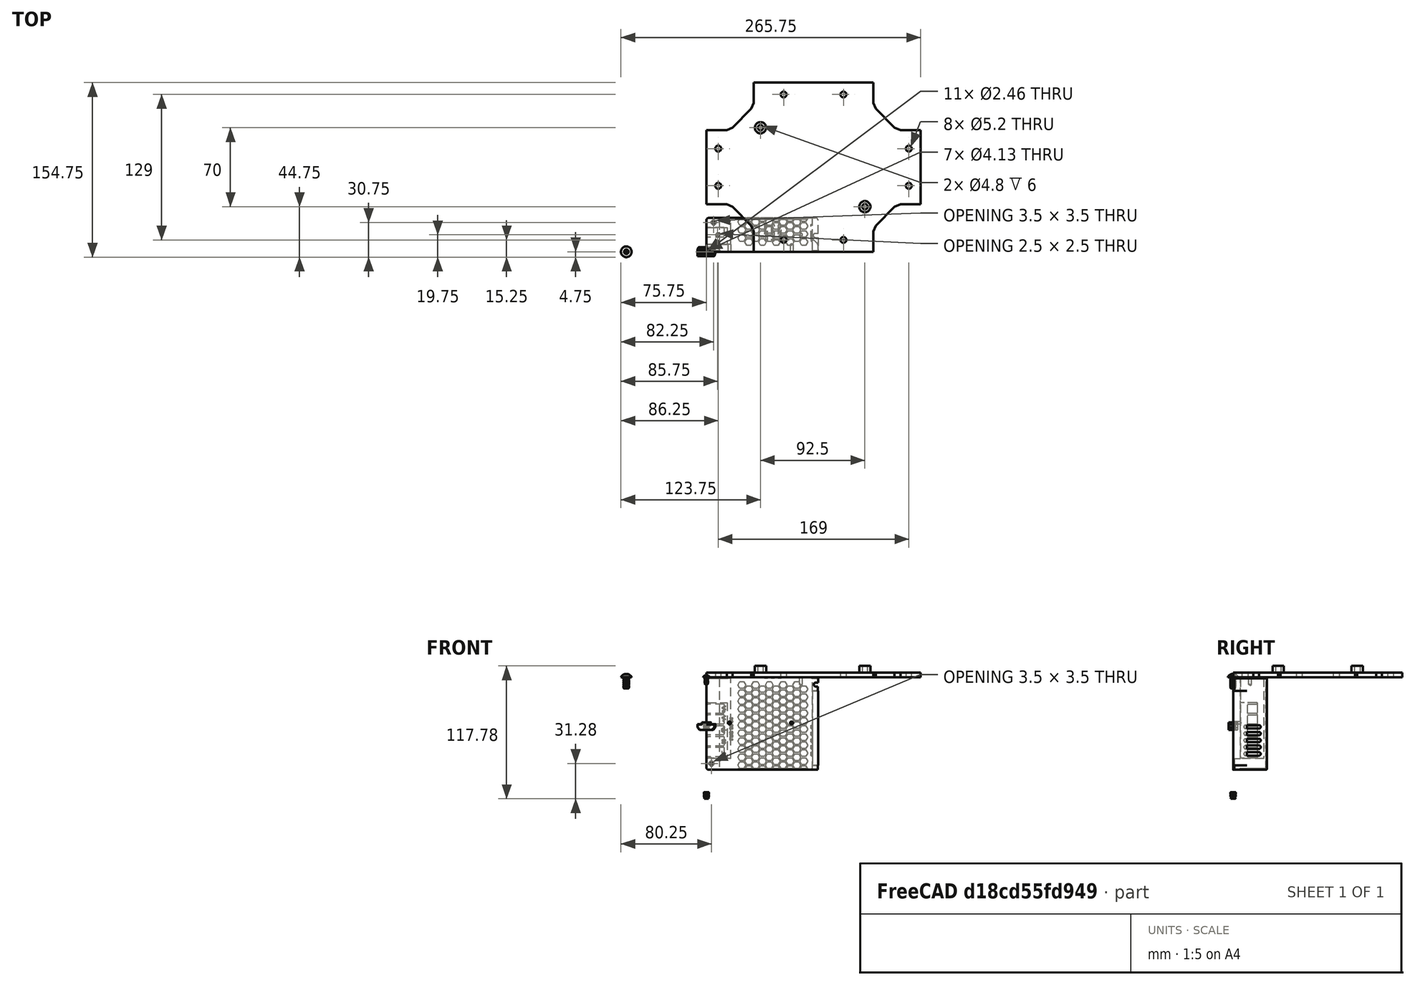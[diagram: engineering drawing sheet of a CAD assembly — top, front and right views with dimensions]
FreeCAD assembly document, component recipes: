
FREECAD ASSEMBLY — COMPONENT RECIPES ("psu-mount")

This assembly document has 14 components, labeled P0..P13 below (a component is one placed body or linked part). 1 of them carries a construction recipe — the FreeCAD feature program that regenerates the part from scratch, quoted from this document or its linked companion documents; the rest are supplied as boundary geometry only. No exploded tour is included for this assembly.
COMPONENT P0 — geometry summary ("M3x5.74-Insert001"; no construction recipe available for this part):
  bounding box: 5.7 x 4.6 x 4.5 mm
  tessellated surface: 13,418 triangles
  volume: 43 mm^3 (36% of its bounding box)
COMPONENT P1 — geometry summary ("M3x5.74-Insert002"; no construction recipe available for this part):
  bounding box: 5.7 x 4.6 x 4.5 mm
  tessellated surface: 13,418 triangles
  volume: 43 mm^3 (36% of its bounding box)
COMPONENT P2 — geometry summary ("M3x6-Screw001"; no construction recipe available for this part):
  bounding box: 7.6 x 5.7 x 5.7 mm
  tessellated surface: 15,240 triangles
  volume: 57 mm^3 (23% of its bounding box)
COMPONENT P3 — geometry summary ("M3x6-Screw002"; no construction recipe available for this part):
  bounding box: 7.6 x 5.7 x 5.7 mm
  tessellated surface: 15,240 triangles
  volume: 57 mm^3 (23% of its bounding box)
COMPONENT P4 — geometry summary ("M5x10-Screw001"; no construction recipe available for this part):
  bounding box: 12.8 x 9.5 x 9.5 mm
  tessellated surface: 23,732 triangles
  volume: 267 mm^3 (23% of its bounding box)
  symmetry: revolution-symmetric about the z axis through its bounding-box center
COMPONENT P5 — geometry summary ("M5x10-Screw003"; no construction recipe available for this part):
  bounding box: 12.8 x 9.5 x 9.5 mm
  tessellated surface: 23,732 triangles
  volume: 267 mm^3 (23% of its bounding box)
  symmetry: revolution-symmetric about the z axis through its bounding-box center
COMPONENT P6 — geometry summary ("M5x10-Screw004"; no construction recipe available for this part):
  bounding box: 12.8 x 9.5 x 9.5 mm
  tessellated surface: 23,732 triangles
  volume: 267 mm^3 (23% of its bounding box)
  symmetry: revolution-symmetric about the z axis through its bounding-box center
COMPONENT P7 — geometry summary ("M5x10-Screw005"; no construction recipe available for this part):
  bounding box: 12.8 x 9.5 x 9.5 mm
  tessellated surface: 23,732 triangles
  volume: 267 mm^3 (23% of its bounding box)
  symmetry: revolution-symmetric about the z axis through its bounding-box center
COMPONENT P8 — geometry summary ("M5x10-Screw006"; no construction recipe available for this part):
  bounding box: 12.8 x 9.5 x 9.5 mm
  tessellated surface: 23,732 triangles
  volume: 267 mm^3 (23% of its bounding box)
  symmetry: revolution-symmetric about the z axis through its bounding-box center
COMPONENT P9 — geometry summary ("M5x10-Screw007"; no construction recipe available for this part):
  bounding box: 12.8 x 9.5 x 9.5 mm
  tessellated surface: 23,732 triangles
  volume: 267 mm^3 (23% of its bounding box)
  symmetry: revolution-symmetric about the z axis through its bounding-box center
COMPONENT P10 — geometry summary ("M5x10-Screw008"; no construction recipe available for this part):
  bounding box: 12.8 x 9.5 x 9.5 mm
  tessellated surface: 23,732 triangles
  volume: 267 mm^3 (23% of its bounding box)
  symmetry: revolution-symmetric about the z axis through its bounding-box center
COMPONENT P11 — geometry summary ("M5x10-Screw009"; no construction recipe available for this part):
  bounding box: 12.8 x 9.5 x 9.5 mm
  tessellated surface: 23,732 triangles
  volume: 267 mm^3 (23% of its bounding box)
  symmetry: revolution-symmetric about the z axis through its bounding-box center
COMPONENT P12 — geometry summary ("MW LRS-50-025"; no construction recipe available for this part):
  bounding box: 99.0 x 82.0 x 30.0 mm
  tessellated surface: 16,878 triangles
  volume: 199954 mm^3 (82% of its bounding box)
COMPONENT P13 — recipe-attached ("mount001", modeled in this document).
Construction recipe (the document's own serialized feature program — sketch geometry with constraints, then the solid features built on it; lengths are millimeters unless a unit is written):

FEATURE [Sketcher::SketchObject] Sketch
  ArcFitTolerance = 1e-06
  AttachmentSupport = -> [XY_Plane]
  FullyConstrained = true
  MakeInternals = false
  MapMode = 5
  sketch-geometry (56):
    g0: LineSegment [constr] StartX=0 StartY=0 StartZ=0 EndX=190 EndY=0 EndZ=0
    g1: LineSegment [constr] StartX=190 StartY=0 StartZ=0 EndX=190 EndY=150 EndZ=0
    g2: LineSegment [constr] StartX=190 StartY=150 StartZ=0 EndX=0 EndY=150 EndZ=0
    g3: LineSegment [constr] StartX=0 StartY=150 StartZ=0 EndX=0 EndY=0 EndZ=0
    g4: LineSegment [constr] StartX=0 StartY=0 StartZ=0 EndX=42 EndY=0 EndZ=0
    g5: LineSegment [constr] StartX=42 StartY=0 StartZ=0 EndX=42 EndY=42 EndZ=0
    g6: LineSegment [constr] StartX=42 StartY=42 StartZ=0 EndX=0 EndY=42 EndZ=0
    g7: LineSegment [constr] StartX=0 StartY=42 StartZ=0 EndX=0 EndY=0 EndZ=0
    g8: LineSegment [constr] StartX=0 StartY=150 StartZ=0 EndX=0 EndY=108 EndZ=0
    g9: LineSegment [constr] StartX=0 StartY=108 StartZ=0 EndX=42 EndY=108 EndZ=0
    g10: LineSegment [constr] StartX=42 StartY=108 StartZ=0 EndX=42 EndY=150 EndZ=0
    g11: LineSegment [constr] StartX=42 StartY=150 StartZ=0 EndX=0 EndY=150 EndZ=0
    g12: LineSegment [constr] StartX=190 StartY=150 StartZ=0 EndX=148 EndY=150 EndZ=0
    g13: LineSegment [constr] StartX=148 StartY=150 StartZ=0 EndX=148 EndY=108 EndZ=0
    g14: LineSegment [constr] StartX=148 StartY=108 StartZ=0 EndX=190 EndY=108 EndZ=0
    g15: LineSegment [constr] StartX=190 StartY=108 StartZ=0 EndX=190 EndY=150 EndZ=0
    g16: LineSegment [constr] StartX=190 StartY=0 StartZ=0 EndX=190 EndY=42 EndZ=0
    g17: LineSegment [constr] StartX=190 StartY=42 StartZ=0 EndX=148 EndY=42 EndZ=0
    g18: LineSegment [constr] StartX=148 StartY=42 StartZ=0 EndX=148 EndY=0 EndZ=0
    g19: LineSegment [constr] StartX=148 StartY=0 StartZ=0 EndX=190 EndY=0 EndZ=0
    g20: LineSegment StartX=42 StartY=129 StartZ=0 EndX=21 EndY=108 EndZ=0
    g21: LineSegment StartX=21 StartY=108 StartZ=0 EndX=0 EndY=108 EndZ=0
    g22: LineSegment StartX=0 StartY=108 StartZ=0 EndX=0 EndY=42 EndZ=0
    g23: LineSegment StartX=0 StartY=42 StartZ=0 EndX=21 EndY=42 EndZ=0
    g24: LineSegment StartX=21 StartY=42 StartZ=0 EndX=42 EndY=21 EndZ=0
    g25: LineSegment StartX=42 StartY=21 StartZ=0 EndX=42 EndY=0 EndZ=0
    g26: LineSegment StartX=42 StartY=0 StartZ=0 EndX=148 EndY=0 EndZ=0
    g27: LineSegment StartX=148 StartY=0 StartZ=0 EndX=148 EndY=21 EndZ=0
    g28: LineSegment StartX=148 StartY=21 StartZ=0 EndX=169 EndY=42 EndZ=0
    g29: LineSegment StartX=169 StartY=42 StartZ=0 EndX=190 EndY=42 EndZ=0
    g30: LineSegment StartX=190 StartY=42 StartZ=0 EndX=190 EndY=108 EndZ=0
    g31: LineSegment StartX=190 StartY=108 StartZ=0 EndX=169 EndY=108 EndZ=0
    g32: LineSegment StartX=169 StartY=108 StartZ=0 EndX=148 EndY=129 EndZ=0
    g33: LineSegment StartX=148 StartY=129 StartZ=0 EndX=148 EndY=150 EndZ=0
    g34: LineSegment StartX=148 StartY=150 StartZ=0 EndX=42 EndY=150 EndZ=0
    g35: LineSegment StartX=42 StartY=150 StartZ=0 EndX=42 EndY=129 EndZ=0
    g36: LineSegment [constr] StartX=95 StartY=129 StartZ=0 EndX=95 EndY=150 EndZ=0
    g37: LineSegment [constr] StartX=95 StartY=139.5 StartZ=0 EndX=42 EndY=139.5 EndZ=0
    g38: Circle CenterX=68.5 CenterY=139.5 CenterZ=0 NormalX=0 NormalY=0 NormalZ=1 AngleXU=0 Radius=2.6
    g39: LineSegment [constr] StartX=95 StartY=139.5 StartZ=0 EndX=148 EndY=139.5 EndZ=0
    g40: Circle CenterX=121.5 CenterY=139.5 CenterZ=0 NormalX=0 NormalY=0 NormalZ=1 AngleXU=0 Radius=2.6
    g41: LineSegment [constr] StartX=0 StartY=75 StartZ=0 EndX=21 EndY=75 EndZ=0
    g42: LineSegment [constr] StartX=10.5 StartY=75 StartZ=0 EndX=10.5 EndY=108 EndZ=0
    g43: LineSegment [constr] StartX=10.5 StartY=75 StartZ=0 EndX=10.5 EndY=42 EndZ=0
    g44: Circle CenterX=10.5 CenterY=91.5 CenterZ=0 NormalX=0 NormalY=0 NormalZ=1 AngleXU=0 Radius=2.6
    g45: Circle CenterX=10.5 CenterY=58.5 CenterZ=0 NormalX=0 NormalY=0 NormalZ=1 AngleXU=0 Radius=2.6
    g46: LineSegment [constr] StartX=95 StartY=21 StartZ=0 EndX=95 EndY=0 EndZ=0
    g47: LineSegment [constr] StartX=95 StartY=10.5 StartZ=0 EndX=42 EndY=10.5 EndZ=0
    g48: LineSegment [constr] StartX=95 StartY=10.5 StartZ=0 EndX=148 EndY=10.5 EndZ=0
    g49: Circle CenterX=68.5 CenterY=10.5 CenterZ=0 NormalX=0 NormalY=0 NormalZ=1 AngleXU=0 Radius=2.6
    g50: Circle CenterX=121.5 CenterY=10.5 CenterZ=0 NormalX=0 NormalY=0 NormalZ=1 AngleXU=0 Radius=2.6
    g51: LineSegment [constr] StartX=169 StartY=75 StartZ=0 EndX=190 EndY=75 EndZ=0
    g52: LineSegment [constr] StartX=179.5 StartY=75 StartZ=0 EndX=179.5 EndY=42 EndZ=0
    g53: LineSegment [constr] StartX=179.5 StartY=75 StartZ=0 EndX=179.5 EndY=108 EndZ=0
    g54: Circle CenterX=179.5 CenterY=91.5 CenterZ=0 NormalX=0 NormalY=0 NormalZ=1 AngleXU=0 Radius=2.6
    g55: Circle CenterX=179.5 CenterY=58.5 CenterZ=0 NormalX=0 NormalY=0 NormalZ=1 AngleXU=0 Radius=2.6
  constraints (127):
    c: Coincident(g0,g1)
    c: Coincident(g1,g2)
    c: Coincident(g2,g3)
    c: Coincident(g3,g0)
    c: Horizontal(g0)
    c: Horizontal(g2)
    c: Vertical(g1)
    c: Vertical(g3)
    c: Distance(g1,g3) = 190
    c: Distance(g0,g2) = 150
    c: Coincident(g0,g-1)
    c: Coincident(g4,g5)
    c: Coincident(g5,g6)
    c: Coincident(g6,g7)
    c: Coincident(g7,g4)
    c: Horizontal(g4)
    c: Horizontal(g6)
    c: Vertical(g5)
    c: Vertical(g7)
    c: Distance(g5,g7) = 42
    c: Distance(g4,g6) = 42
    c: Coincident(g4,g0)
    c: Coincident(g8,g9)
    c: Coincident(g9,g10)
    c: Coincident(g10,g11)
    c: Coincident(g11,g8)
    c: Vertical(g8)
    c: Vertical(g10)
    c: Horizontal(g9)
    c: Horizontal(g11)
    c: Distance(g8,g10) = 42
    c: Distance(g9,g11) = 42
    c: Coincident(g8,g2)
    c: Coincident(g12,g13)
    c: Coincident(g13,g14)
    c: Coincident(g14,g15)
    c: Coincident(g15,g12)
    c: Horizontal(g12)
    c: Horizontal(g14)
    c: Vertical(g13)
    c: Vertical(g15)
    c: Distance(g13,g15) = 42
    c: Distance(g12,g14) = 42
    c: Coincident(g12,g1)
    c: Coincident(g16,g17)
    c: Coincident(g17,g18)
    c: Coincident(g18,g19)
    c: Coincident(g19,g16)
    c: Vertical(g16)
    c: Vertical(g18)
    c: Horizontal(g17)
    c: Horizontal(g19)
    c: Distance(g16,g18) = 42
    c: Distance(g17,g19) = 42
    c: Coincident(g16,g0)
    c: Symmetric(g10,g10,g20)
    c: Symmetric(g9,g9,g20)
    c: Coincident(g21,g20)
    c: Coincident(g21,g8)
    c: Coincident(g22,g8)
    c: Coincident(g22,g6)
    c: Coincident(g23,g6)
    c: Symmetric(g6,g6,g23)
    c: Coincident(g24,g23)
    c: Symmetric(g5,g5,g24)
    c: Coincident(g25,g24)
    c: Coincident(g25,g4)
    c: Coincident(g26,g4)
    c: Coincident(g26,g18)
    c: Coincident(g27,g18)
    c: Symmetric(g18,g18,g27)
    c: Coincident(g28,g27)
    c: Symmetric(g17,g17,g28)
    c: Coincident(g29,g28)
    c: Coincident(g29,g16)
    c: Coincident(g30,g16)
    c: Coincident(g30,g14)
    c: Coincident(g31,g14)
    c: Symmetric(g14,g14,g31)
    c: Coincident(g32,g31)
    c: Symmetric(g13,g13,g32)
    c: Coincident(g33,g32)
    c: Coincident(g33,g12)
    c: Coincident(g34,g12)
    c: Coincident(g34,g10)
    c: Coincident(g35,g10)
    c: Coincident(g35,g20)
    c: Symmetric(g20,g32,g36)
    c: Symmetric(g34,g34,g36)
    c: Symmetric(g36,g36,g37)
    c: Symmetric(g35,g35,g37)
    c: Diameter(g38) = 5.2
    c: Symmetric(g37,g37,g38)
    c: Coincident(g39,g37)
    c: Symmetric(g33,g33,g39)
    c: Diameter(g40) = 5.2
    c: Symmetric(g39,g39,g40)
    c: Symmetric(g22,g22,g41)
    c: Symmetric(g20,g23,g41)
    c: Symmetric(g41,g41,g42)
    c: Symmetric(g21,g21,g42)
    c: Coincident(g43,g42)
    c: Symmetric(g23,g23,g43)
    c: Diameter(g44) = 5.2
    c: Symmetric(g42,g42,g44)
    c: Diameter(g45) = 5.2
    c: Symmetric(g43,g43,g45)
    c: Symmetric(g24,g27,g46)
    c: Symmetric(g26,g26,g46)
    c: Symmetric(g46,g46,g47)
    c: Symmetric(g25,g25,g47)
    c: Coincident(g48,g47)
    c: Symmetric(g27,g27,g48)
    c: Diameter(g49) = 5.2
    c: Symmetric(g47,g47,g49)
    c: Diameter(g50) = 5.2
    c: Symmetric(g48,g48,g50)
    c: Symmetric(g31,g28,g51)
    c: Symmetric(g30,g30,g51)
    c: Symmetric(g51,g51,g52)
    c: Symmetric(g29,g29,g52)
    c: Coincident(g53,g52)
    c: Symmetric(g31,g31,g53)
    c: Diameter(g54) = 5.2
    c: Symmetric(g53,g53,g54)
    c: Diameter(g55) = 5.2
    c: Symmetric(g52,g52,g55)
FEATURE [PartDesign::Pad] Pad
  Direction = (0,0,1)
  Length = 4
  Length2 = 10
  Profile = -> Sketch
  ReferenceAxis = -> Sketch [N_Axis]
  Refine = true
  Suppressed = false
  Type = 0
FEATURE [PartDesign::Chamfer] Chamfer
  Angle = 45
  Base = -> Pad [Edge1,Edge2,Edge11,Edge14,Edge23,Edge26,Edge38,Edge35]
  BaseFeature = -> Pad
  ChamferType = 0
  FlipDirection = false
  Refine = true
  Size = 3
  Size2 = 1
  SupportTransform = false
  Suppressed = false
  UseAllEdges = false
FEATURE [Sketcher::SketchObject] Sketch001
  ArcFitTolerance = 1e-06
  AttachmentSupport = -> [Chamfer]
  FullyConstrained = true
  MakeInternals = false
  MapMode = 5
  Placement = pos=(0,0,4) rot=(0,0,1;0rad)
  sketch-geometry (16):
    g0: LineSegment [constr] StartX=0 StartY=0 StartZ=0 EndX=190 EndY=0 EndZ=0
    g1: LineSegment [constr] StartX=190 StartY=0 StartZ=0 EndX=190 EndY=150 EndZ=0
    g2: LineSegment [constr] StartX=190 StartY=150 StartZ=0 EndX=0 EndY=150 EndZ=0
    g3: LineSegment [constr] StartX=0 StartY=150 StartZ=0 EndX=0 EndY=0 EndZ=0
    g4: LineSegment [constr] StartX=0 StartY=150 StartZ=0 EndX=0 EndY=110 EndZ=0
    g5: LineSegment [constr] StartX=0 StartY=110 StartZ=0 EndX=48 EndY=110 EndZ=0
    g6: LineSegment [constr] StartX=48 StartY=110 StartZ=0 EndX=48 EndY=150 EndZ=0
    g7: LineSegment [constr] StartX=48 StartY=150 StartZ=0 EndX=0 EndY=150 EndZ=0
    g8: Circle CenterX=48 CenterY=110 CenterZ=0 NormalX=0 NormalY=0 NormalZ=1 AngleXU=0 Radius=5
    g9: Circle CenterX=48 CenterY=110 CenterZ=0 NormalX=0 NormalY=0 NormalZ=1 AngleXU=0 Radius=2.4
    g10: LineSegment [constr] StartX=48 StartY=110 StartZ=0 EndX=48 EndY=40 EndZ=0
    g11: LineSegment [constr] StartX=48 StartY=40 StartZ=0 EndX=140.5 EndY=40 EndZ=0
    g12: LineSegment [constr] StartX=140.5 StartY=40 StartZ=0 EndX=140.5 EndY=110 EndZ=0
    g13: LineSegment [constr] StartX=140.5 StartY=110 StartZ=0 EndX=48 EndY=110 EndZ=0
    g14: Circle CenterX=140.5 CenterY=40 CenterZ=0 NormalX=0 NormalY=0 NormalZ=1 AngleXU=0 Radius=2.4
    g15: Circle CenterX=140.5 CenterY=40 CenterZ=0 NormalX=0 NormalY=0 NormalZ=1 AngleXU=0 Radius=5
  constraints (41):
    c: Coincident(g0,g1)
    c: Coincident(g1,g2)
    c: Coincident(g2,g3)
    c: Coincident(g3,g0)
    c: Horizontal(g0)
    c: Horizontal(g2)
    c: Vertical(g1)
    c: Vertical(g3)
    c: Distance(g1,g3) = 190
    c: Distance(g0,g2) = 150
    c: Coincident(g0,g-1)
    c: Coincident(g4,g5)
    c: Coincident(g5,g6)
    c: Coincident(g6,g7)
    c: Coincident(g7,g4)
    c: Vertical(g4)
    c: Vertical(g6)
    c: Horizontal(g5)
    c: Horizontal(g7)
    c: Distance(g4,g6) = 48
    c: Distance(g5,g7) = 40
    c: Coincident(g4,g2)
    c: Diameter(g8) = 10
    c: Coincident(g8,g5)
    c: Diameter(g9) = 4.8
    c: Coincident(g9,g5)
    c: Coincident(g10,g11)
    c: Coincident(g11,g12)
    c: Coincident(g12,g13)
    c: Coincident(g13,g10)
    c: Vertical(g10)
    c: Vertical(g12)
    c: Horizontal(g11)
    c: Horizontal(g13)
    c: Distance(g10,g12) = 92.5
    c: Distance(g11,g13) = 70
    c: Coincident(g10,g5)
    c: Diameter(g14) = 4.8
    c: Coincident(g14,g11)
    c: Diameter(g15) = 10
    c: Coincident(g15,g11)
FEATURE [PartDesign::Pad] Pad001
  BaseFeature = -> Chamfer
  Direction = (0,0,1)
  Length = 6
  Length2 = 10
  Profile = -> Sketch001
  ReferenceAxis = -> Sketch001 [N_Axis]
  Refine = true
  Suppressed = false
  Type = 0
FEATURE [PartDesign::Body] Body  label="mount"
  AllowCompound = false
  Group = -> [Sketch,Pad,Chamfer,Sketch001,Pad001]
  Origin = -> Origin
  Tip = -> Pad001
PROVENANCE & LICENSES
A FreeCAD (.FCStd) document from a public repository crawl; recipes are the document's own serialized feature recipes (and, for linked parts, companion documents' recipes).
License: other.
